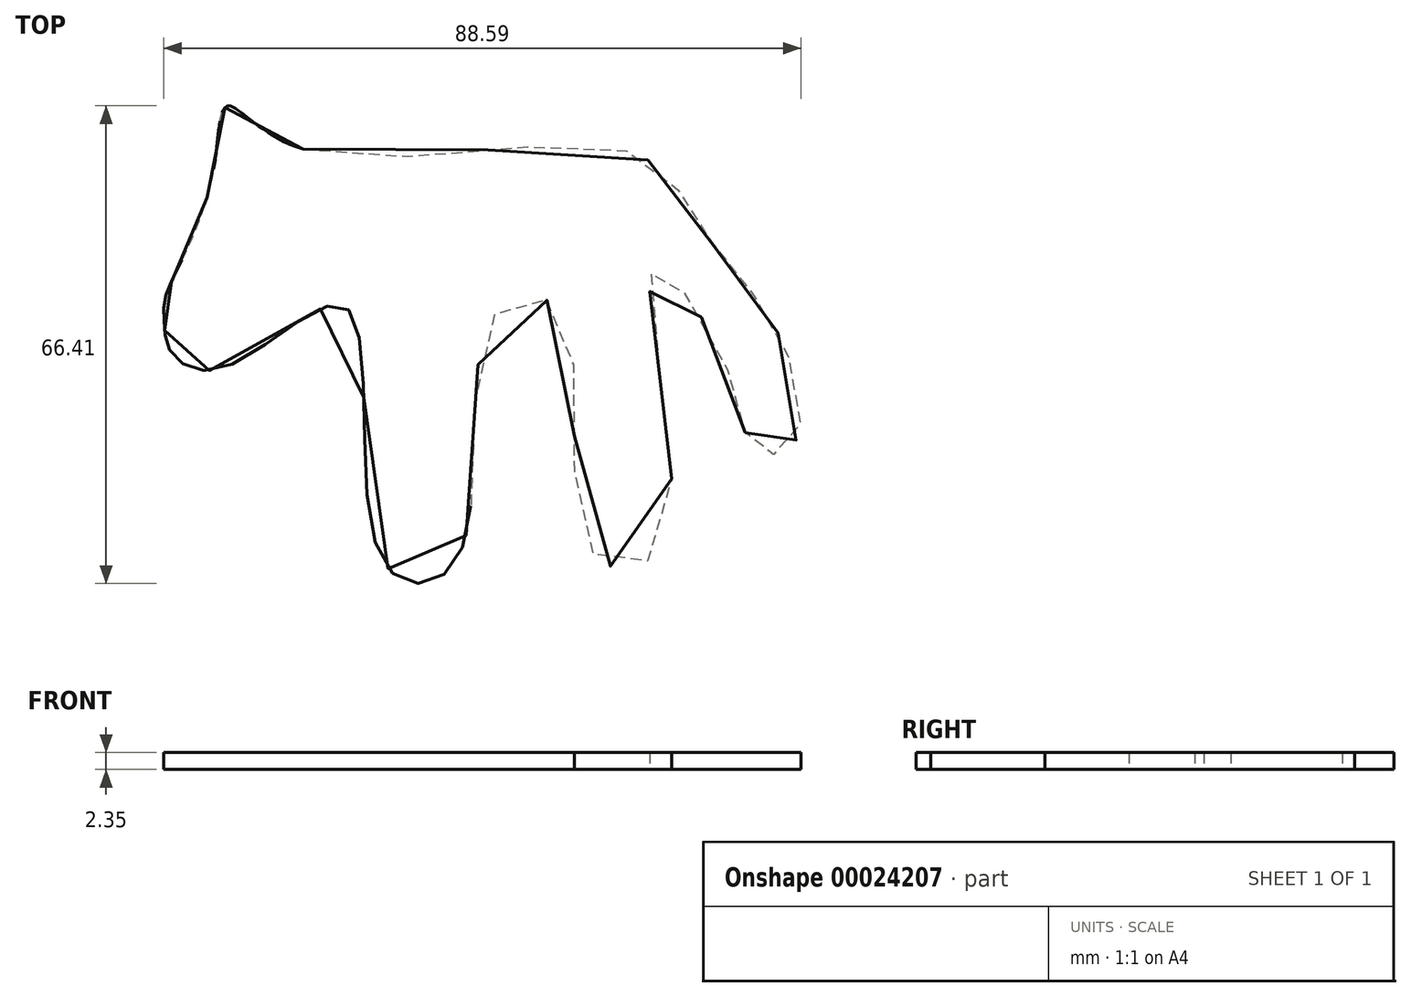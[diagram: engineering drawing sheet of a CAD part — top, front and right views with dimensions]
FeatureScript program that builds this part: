
annotation { "Feature Type Name" : "Feature", "Feature Type Description" : "" }
export const myFeature = defineFeature(function(context is Context, id is Id, definition is map)
    precondition{}
    {
        {
            var Q0;
            Q0=qCreatedBy(makeId("Top.planeOp"),FACE);
            var sketch = newSketch(context, id + "F0", { "sketchPlane" : qUnion([Q0])});
            skFitSpline(sketch, "E0", {"points": [v(-48.9, 37.63) * mm, v(-3.8, 37.36) * mm, v(6.8, 26.22) * mm, v(17.12, 12.09) * mm, v(19.29, -3.4) * mm, v(14.13, -4.21) * mm, v(10.05, 7.2) * mm, v(-0.27, 20.78) * mm, v(1.09, -16.98) * mm, v(-8.97, -18.07) * mm, v(-13.04, 14.8) * mm, v(-22.55, 14.26) * mm, v(-27.71, -19.7) * mm, v(-37.76, -19.7) * mm, v(-42.93, 15.62) * mm, v(-60.04, 7.2) * mm, v(-67.38, 9.64) * mm, v(-68.2, 13.45) * mm, v(-68.2, 16.44) * mm, v(-66.3, 21.06) * mm, v(-61.4, 34.37) * mm, v(-59.5, 43.6) * mm, v(-48.9, 37.63) * mm]});
            skSolve(sketch);
        }
        {
            var Q0;
            Q0 = qSketchRegion(id + "F0", true);
            extrude(context, id + "F1", {"entities" : qUnion([Q0]), "depth" : 2.35 * mm});
        }
    });
